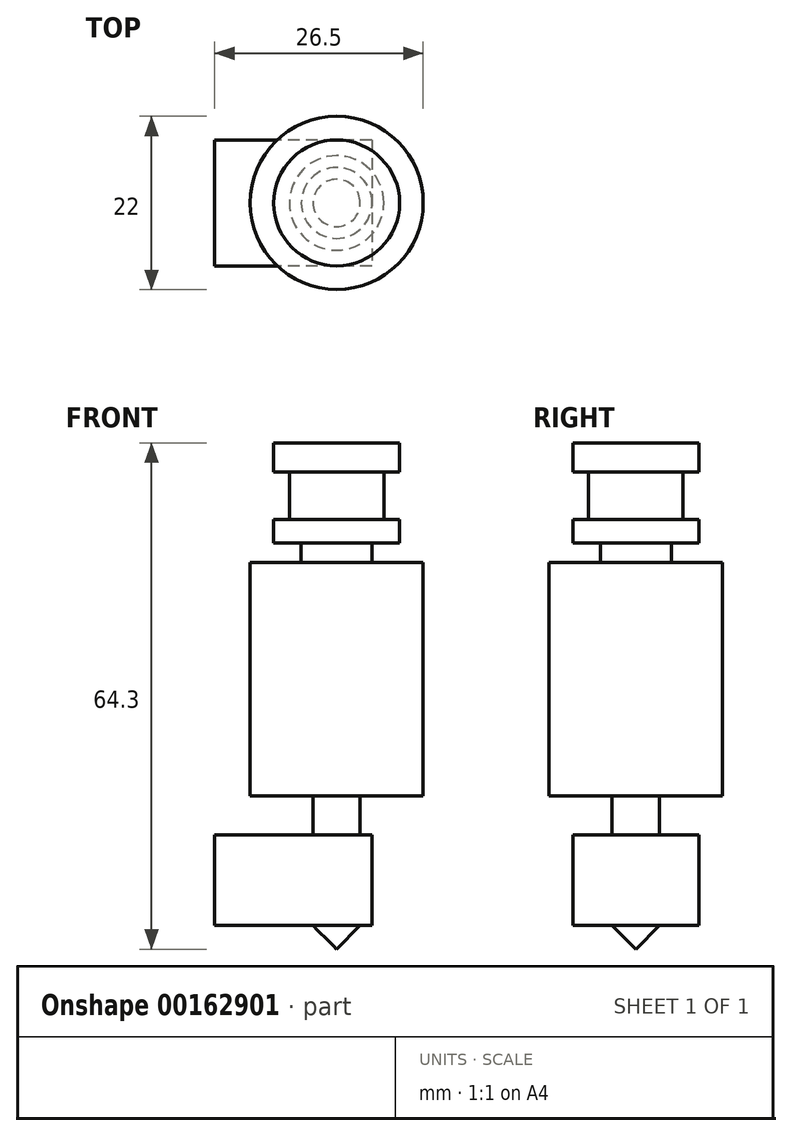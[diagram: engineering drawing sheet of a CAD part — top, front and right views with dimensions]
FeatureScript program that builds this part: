
annotation { "Feature Type Name" : "Feature", "Feature Type Description" : "" }
export const myFeature = defineFeature(function(context is Context, id is Id, definition is map)
    precondition{}
    {
        {
            var Q0;
            Q0=qCreatedBy(makeId("Front.planeOp"),FACE);
            var sketch = newSketch(context, id + "F0", { "sketchPlane" : qUnion([Q0])});
            skLineSegment(sketch, "E0", {"start": v(0, 0) * mm, "end": v(0, -49.8) * mm});
            skLineSegment(sketch, "E1", {"start": v(0, 0) * mm, "end": v(-8, 0) * mm});
            skLineSegment(sketch, "E2", {"start": v(-8, 0) * mm, "end": v(-8, -3.7) * mm});
            skLineSegment(sketch, "E3", {"start": v(-8, -3.7) * mm, "end": v(-6, -3.7) * mm});
            skLineSegment(sketch, "E4", {"start": v(-6, -3.7) * mm, "end": v(-6, -9.7) * mm});
            skLineSegment(sketch, "E5", {"start": v(-6, -9.7) * mm, "end": v(-8, -9.7) * mm});
            skLineSegment(sketch, "E6", {"start": v(-8, -9.7) * mm, "end": v(-8, -12.7) * mm});
            skLineSegment(sketch, "E7", {"start": v(-8, -12.7) * mm, "end": v(-4.5, -12.7) * mm});
            skLineSegment(sketch, "E8", {"start": v(-4.5, -12.7) * mm, "end": v(-4.5, -15.2) * mm});
            skLineSegment(sketch, "E9", {"start": v(-4.5, -15.2) * mm, "end": v(-11, -15.2) * mm});
            skLineSegment(sketch, "E10", {"start": v(-11, -15.2) * mm, "end": v(-11, -44.8) * mm});
            skLineSegment(sketch, "E11", {"start": v(-11, -44.8) * mm, "end": v(-3, -44.8) * mm});
            skLineSegment(sketch, "E12", {"start": v(-3, -44.8) * mm, "end": v(-3, -49.8) * mm});
            skLineSegment(sketch, "E13", {"start": v(-3, -49.8) * mm, "end": v(0, -49.8) * mm});
            skSolve(sketch);
        }
        {
            var Q0;
            Q0=makeQuery(id+"F0.imprint","IMPRINT",FACE,{"disambiguationData":[TD([[makeQuery(id+"F0.imprint","IMPRINT",EDGE,{"derivedFrom":sQuery(id+"F0.wireOp",EDGE,"E0")}),-1.0]])]});
            var Q1;
            Q1 = qConstructionFilter(qBodyType(qCreatedBy(id + "F0" ,EDGE), BodyType.WIRE), ConstructionObject.NO);
            var Q2;
            Q2=sQuery(id+"F0.wireOp",EDGE,"E0");
            revolve(context, id + "F1", {"entities" : qUnion([Q0]), "surfaceEntities" : qUnion([Q1]), "axis" : qUnion([Q2]), "revolveType" : RevolveType.FULL});
        }
        {
            var Q0;
            Q0=makeQuery(id+"F1.opRevolve","SWEPT_FACE",FACE,{"disambiguationData":[OSD([sQuery(id+"F0.wireOp",EDGE,"E13")])]});
            var sketch = newSketch(context, id + "F2", { "sketchPlane" : qUnion([Q0])});
            skLineSegment(sketch, "E14.bottom", {"start": v(4.5, -8) * mm, "end": v(-15.5, -8) * mm});
            skLineSegment(sketch, "E14.top", {"start": v(4.5, 8) * mm, "end": v(-15.5, 8) * mm});
            skLineSegment(sketch, "E14.left", {"start": v(4.5, -8) * mm, "end": v(4.5, 8) * mm});
            skLineSegment(sketch, "E14.right", {"start": v(-15.5, -8) * mm, "end": v(-15.5, 8) * mm});
            skPoint(sketch, "E14.middle", {"position": v(-5.5, 0) * mm});
            skSolve(sketch);
        }
        {
            var Q0;
            Q0 = qSketchRegion(id + "F2", true);
            extrude(context, id + "F3", {"entities" : qUnion([Q0]), "operationType" : NewBodyOperationType.ADD, "depth" : 11.5 * mm});
        }
        {
            var Q0;
            Q0=makeQuery(id+"F3.opExtrude","CAP_FACE",FACE,{"disambiguationData":[OSD([sQuery(id+"F2.wireOp",EDGE,"E14.bottom"),sQuery(id+"F2.wireOp",EDGE,"E14.top"),sQuery(id+"F2.wireOp",EDGE,"E14.left"),sQuery(id+"F2.wireOp",EDGE,"E14.right")])],"isStart":false});
            var sketch = newSketch(context, id + "F4", { "sketchPlane" : qUnion([Q0])});
            skCircle(sketch, "E15", {"center": v(0, 0) * mm, "radius": 3 * mm});
            skSolve(sketch);
        }
        {
            var Q0;
            Q0 = qSketchRegion(id + "F4", true);
            extrude(context, id + "F5", {"entities" : qUnion([Q0]), "operationType" : NewBodyOperationType.ADD, "depth" : 5 * mm, "hasDraft" : true, "draftAngle" : 45 * degree, "draftPullDirection" : true});
        }
    });
